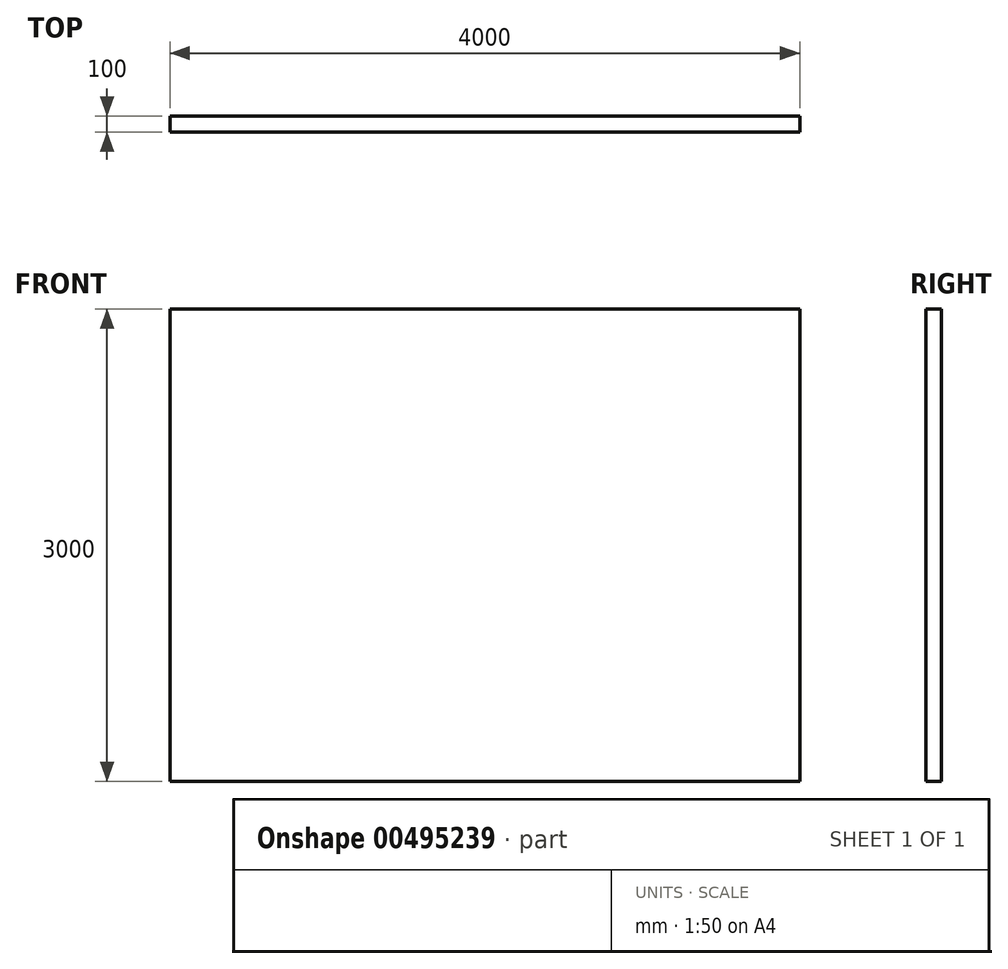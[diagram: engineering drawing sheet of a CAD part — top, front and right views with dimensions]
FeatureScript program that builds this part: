
annotation { "Feature Type Name" : "Feature", "Feature Type Description" : "" }
export const myFeature = defineFeature(function(context is Context, id is Id, definition is map)
    precondition{}
    {
        {
            var Q0;
            Q0=qCreatedBy(makeId("Front.planeOp"),FACE);
            var sketch = newSketch(context, id + "F0", { "sketchPlane" : qUnion([Q0])});
            skLineSegment(sketch, "E0.bottom", {"start": v(0, 0) * mm, "end": v(4000, 0) * mm});
            skLineSegment(sketch, "E0.top", {"start": v(0, 3000) * mm, "end": v(4000, 3000) * mm});
            skLineSegment(sketch, "E0.left", {"start": v(0, 0) * mm, "end": v(0, 3000) * mm});
            skLineSegment(sketch, "E0.right", {"start": v(4000, 0) * mm, "end": v(4000, 3000) * mm});
            skSolve(sketch);
        }
        {
            var Q0;
            Q0=makeQuery(id+"F0.imprint","IMPRINT",FACE,{"disambiguationData":[TD([[makeQuery(id+"F0.imprint","IMPRINT",EDGE,{"derivedFrom":sQuery(id+"F0.wireOp",EDGE,"E0.bottom")}),1.0]])]});
            extrude(context, id + "F1", {"entities" : qUnion([Q0]), "depth" : 100 * mm});
        }
    });
